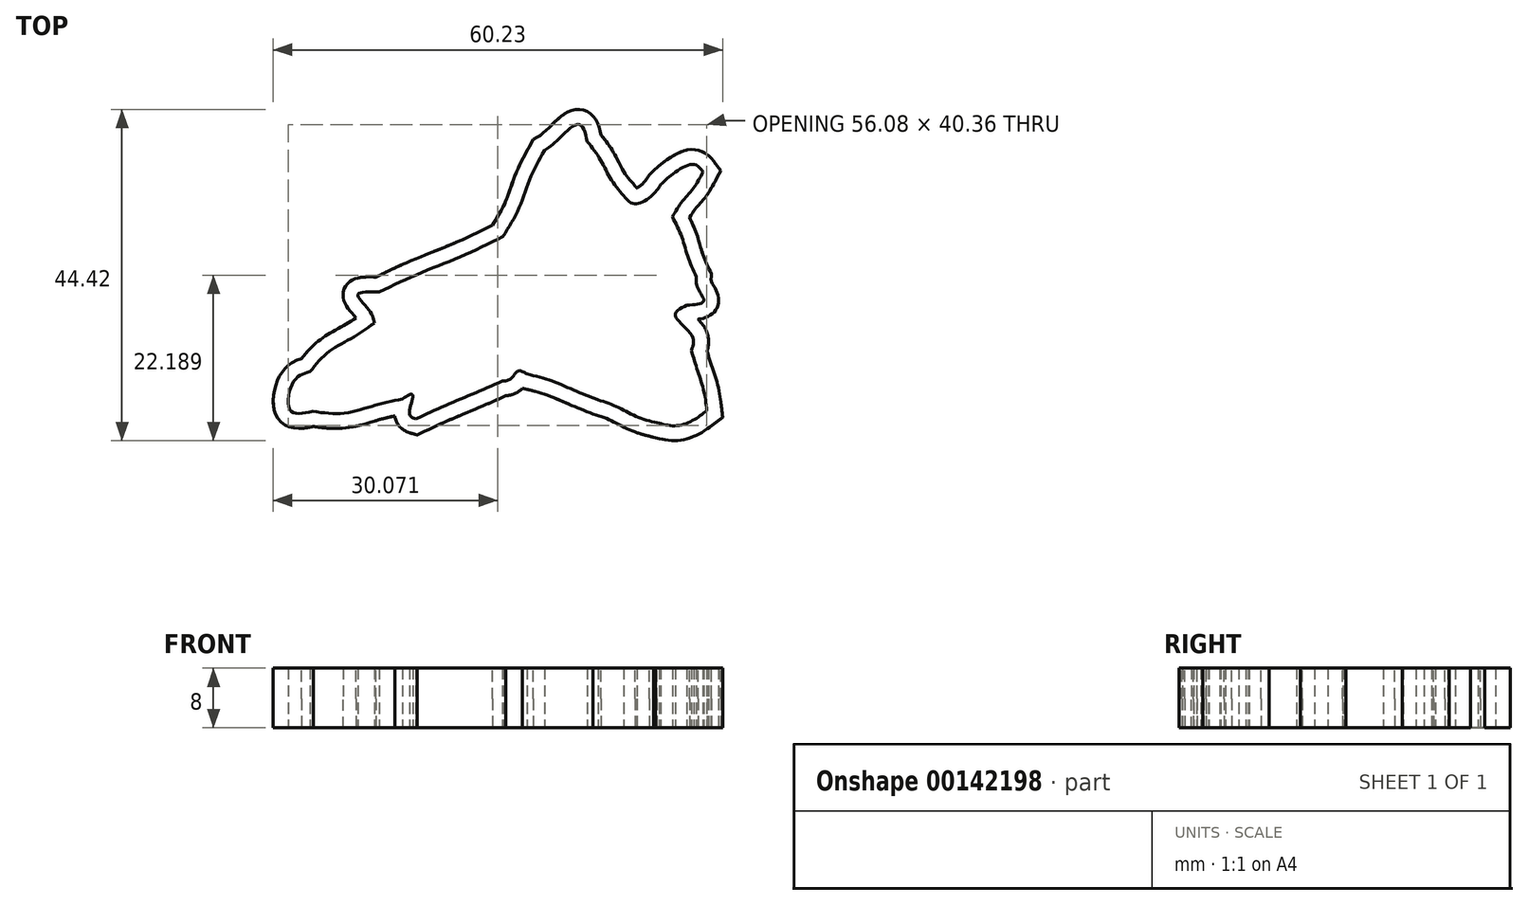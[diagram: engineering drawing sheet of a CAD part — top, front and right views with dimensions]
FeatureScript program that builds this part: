
annotation { "Feature Type Name" : "Feature", "Feature Type Description" : "" }
export const myFeature = defineFeature(function(context is Context, id is Id, definition is map)
    precondition{}
    {
        {
            var Q0;
            Q0=qCreatedBy(makeId("Top.planeOp"),FACE);
            var sketch = newSketch(context, id + "F0", { "sketchPlane" : qUnion([Q0])});
            skFitSpline(sketch, "E0", {"points": [v(207.98, -192.64) * mm, v(180.99, -184.62) * mm, v(155.3, -171.77) * mm, v(128.78, -161.9) * mm]});
            skFitSpline(sketch, "E1", {"points": [v(128.78, -161.9) * mm, v(97.41, -149.3) * mm, v(66.22, -136.29) * mm, v(33.65, -127.28) * mm]});
            skFitSpline(sketch, "E2", {"points": [v(33.65, -127.28) * mm, v(21.66, -123.25) * mm, v(11.66, -133.84) * mm, v(0.62, -136.7) * mm]});
            skFitSpline(sketch, "E3", {"points": [v(0.62, -136.7) * mm, v(-38.12, -153.64) * mm, v(-77.1, -170.06) * mm, v(-115.57, -187.57) * mm]});
            skFitSpline(sketch, "E4", {"points": [v(-115.57, -187.57) * mm, v(-123.77, -180.92) * mm, v(-119.85, -155.13) * mm, v(-133.48, -160.64) * mm]});
            skFitSpline(sketch, "E5", {"points": [v(-133.48, -160.64) * mm, v(-172.62, -170.05) * mm, v(-212.95, -179.94) * mm, v(-253.4, -177.34) * mm]});
            skFitSpline(sketch, "E6", {"points": [v(-253.4, -177.34) * mm, v(-283.5, -175.85) * mm, v(-278.66, -136.68) * mm, v(-257.19, -124.2) * mm]});
            skFitSpline(sketch, "E7", {"points": [v(-257.19, -124.2) * mm, v(-232.27, -97.76) * mm, v(-200.98, -79.07) * mm, v(-171.08, -59.07) * mm]});
            skFitSpline(sketch, "E8", {"points": [v(-171.08, -59.07) * mm, v(-177.57, -42.24) * mm, v(-192.94, -21.02) * mm, v(-164.68, -17.5) * mm]});
            skFitSpline(sketch, "E9", {"points": [v(-164.68, -17.5) * mm, v(-109.73, 8) * mm, v(-53.29, 30.82) * mm, v(1.22, 56.87) * mm]});
            skFitSpline(sketch, "E10", {"points": [v(1.22, 56.87) * mm, v(22.3, 94.12) * mm, v(37.5, 134.5) * mm, v(56.87, 172.55) * mm]});
            skFitSpline(sketch, "E11", {"points": [v(56.87, 172.55) * mm, v(71.2, 183.15) * mm, v(102.82, 207.47) * mm, v(114.38, 184.26) * mm]});
            skFitSpline(sketch, "E12", {"points": [v(114.38, 184.26) * mm, v(131.65, 160.66) * mm, v(145.7, 134.5) * mm, v(163.45, 111.5) * mm]});
            skFitSpline(sketch, "E13", {"points": [v(163.45, 111.5) * mm, v(178.1, 100.76) * mm, v(201, 112.12) * mm, v(212.98, 126.63) * mm]});
            skFitSpline(sketch, "E14", {"points": [v(212.98, 126.63) * mm, v(225.98, 138.5) * mm, v(255.9, 153.74) * mm, v(269.56, 143.47) * mm]});
            skFitSpline(sketch, "E15", {"points": [v(269.56, 143.47) * mm, v(257.2, 122.68) * mm, v(241.52, 103.8) * mm, v(228.38, 83.44) * mm]});
            skFitSpline(sketch, "E16", {"points": [v(228.38, 83.44) * mm, v(240.74, 57.28) * mm, v(249.34, 29.67) * mm, v(260.41, 3) * mm]});
            skFitSpline(sketch, "E17", {"points": [v(260.41, 3) * mm, v(262.58, -12.54) * mm, v(270.34, -29.44) * mm, v(247.92, -35.02) * mm]});
            skFitSpline(sketch, "E18", {"points": [v(247.92, -35.02) * mm, v(232.4, -48.68) * mm, v(254.9, -76.08) * mm, v(253.93, -95.71) * mm]});
            skFitSpline(sketch, "E19", {"points": [v(253.93, -95.71) * mm, v(261.93, -122.2) * mm, v(270.33, -149.05) * mm, v(274.63, -176.4) * mm]});
            skFitSpline(sketch, "E20", {"points": [v(274.63, -176.4) * mm, v(257.37, -188.55) * mm, v(233.43, -196.59) * mm, v(210.62, -193.22) * mm]});
            skLineSegment(sketch, "E21", {"start": v(210.62, -193.22) * mm, "end": v(207.98, -192.64) * mm});
            skLineSegment(sketch, "E22", {"start": v(207.98, -192.64) * mm, "end": v(207.98, -192.64) * mm});
            skLineSegment(sketch, "E23", {"start": v(207.98, -192.64) * mm, "end": v(210.62, -193.22) * mm});
            skSolve(sketch);
        }
        {
            var Q0;
            Q0 = qSketchRegion(id + "F0", true);
            extrude(context, id + "F1", {"entities" : qUnion([Q0]), "depth" : 38.9 * mm});
        }
        {
            var Q0;
            Q0=makeQuery(id+"F1.opExtrude","SWEPT_BODY",BODY,{"disambiguationData":[OSD([sQuery(id+"F0.wireOp",EDGE,"E0"),sQuery(id+"F0.wireOp",EDGE,"E1"),sQuery(id+"F0.wireOp",EDGE,"E2"),sQuery(id+"F0.wireOp",EDGE,"E3"),sQuery(id+"F0.wireOp",EDGE,"E4"),sQuery(id+"F0.wireOp",EDGE,"E5"),sQuery(id+"F0.wireOp",EDGE,"E6"),sQuery(id+"F0.wireOp",EDGE,"E7"),sQuery(id+"F0.wireOp",EDGE,"E8"),sQuery(id+"F0.wireOp",EDGE,"E9"),sQuery(id+"F0.wireOp",EDGE,"E10"),sQuery(id+"F0.wireOp",EDGE,"E11"),sQuery(id+"F0.wireOp",EDGE,"E12"),sQuery(id+"F0.wireOp",EDGE,"E13"),sQuery(id+"F0.wireOp",EDGE,"E14"),sQuery(id+"F0.wireOp",EDGE,"E15"),sQuery(id+"F0.wireOp",EDGE,"E16"),sQuery(id+"F0.wireOp",EDGE,"E17"),sQuery(id+"F0.wireOp",EDGE,"E18"),sQuery(id+"F0.wireOp",EDGE,"E19"),sQuery(id+"F0.wireOp",EDGE,"E20"),sQuery(id+"F0.wireOp",EDGE,"E23")])]});
            var Q1;
            Q1=qCreatedBy(makeId("Origin.pointOp"),VERTEX);
            transform(context, id + "F2", {"entities" : qUnion([Q0]), "transformType" : TransformType.SCALE_UNIFORMLY, "scale" : 0.1, "scalePoint" : qUnion([Q1]), "makeCopy" : false});
        }
        {
            var Q0;
            Q0=makeQuery(id+"F1.opExtrude","CAP_FACE",FACE,{"disambiguationData":[OSD([sQuery(id+"F0.wireOp",EDGE,"E0"),sQuery(id+"F0.wireOp",EDGE,"E1"),sQuery(id+"F0.wireOp",EDGE,"E2"),sQuery(id+"F0.wireOp",EDGE,"E3"),sQuery(id+"F0.wireOp",EDGE,"E4"),sQuery(id+"F0.wireOp",EDGE,"E5"),sQuery(id+"F0.wireOp",EDGE,"E6"),sQuery(id+"F0.wireOp",EDGE,"E7"),sQuery(id+"F0.wireOp",EDGE,"E8"),sQuery(id+"F0.wireOp",EDGE,"E9"),sQuery(id+"F0.wireOp",EDGE,"E10"),sQuery(id+"F0.wireOp",EDGE,"E11"),sQuery(id+"F0.wireOp",EDGE,"E12"),sQuery(id+"F0.wireOp",EDGE,"E13"),sQuery(id+"F0.wireOp",EDGE,"E14"),sQuery(id+"F0.wireOp",EDGE,"E15"),sQuery(id+"F0.wireOp",EDGE,"E16"),sQuery(id+"F0.wireOp",EDGE,"E17"),sQuery(id+"F0.wireOp",EDGE,"E18"),sQuery(id+"F0.wireOp",EDGE,"E19"),sQuery(id+"F0.wireOp",EDGE,"E20"),sQuery(id+"F0.wireOp",EDGE,"E23")])],"isStart":false});
            var Q1;
            Q1=makeQuery(id+"F1.opExtrude","CAP_FACE",FACE,{"disambiguationData":[OSD([sQuery(id+"F0.wireOp",EDGE,"E0"),sQuery(id+"F0.wireOp",EDGE,"E1"),sQuery(id+"F0.wireOp",EDGE,"E2"),sQuery(id+"F0.wireOp",EDGE,"E3"),sQuery(id+"F0.wireOp",EDGE,"E4"),sQuery(id+"F0.wireOp",EDGE,"E5"),sQuery(id+"F0.wireOp",EDGE,"E6"),sQuery(id+"F0.wireOp",EDGE,"E7"),sQuery(id+"F0.wireOp",EDGE,"E8"),sQuery(id+"F0.wireOp",EDGE,"E9"),sQuery(id+"F0.wireOp",EDGE,"E10"),sQuery(id+"F0.wireOp",EDGE,"E11"),sQuery(id+"F0.wireOp",EDGE,"E12"),sQuery(id+"F0.wireOp",EDGE,"E13"),sQuery(id+"F0.wireOp",EDGE,"E14"),sQuery(id+"F0.wireOp",EDGE,"E15"),sQuery(id+"F0.wireOp",EDGE,"E16"),sQuery(id+"F0.wireOp",EDGE,"E17"),sQuery(id+"F0.wireOp",EDGE,"E18"),sQuery(id+"F0.wireOp",EDGE,"E19"),sQuery(id+"F0.wireOp",EDGE,"E20"),sQuery(id+"F0.wireOp",EDGE,"E23")])],"isStart":true});
            shell(context, id + "F3", {"entities" : qUnion([Q0, Q1]), "thickness" : 2 * mm, "oppositeDirection" : true});
        }
        {
            var Q0;
            Q0=qCreatedBy(makeId("Top.planeOp"),FACE);
            cPlane(context, id + "F4", {"entities" : qUnion([Q0]), "cplaneType" : CPlaneType.OFFSET, "offset" : 8 * mm, "width" : 150 * mm, "height" : 150 * mm});
        }
        {
            var Q0;
            Q0=makeQuery(id+"F1.opExtrude","CAP_FACE",FACE,{"disambiguationData":[OSD([sQuery(id+"F0.wireOp",EDGE,"E0"),sQuery(id+"F0.wireOp",EDGE,"E1"),sQuery(id+"F0.wireOp",EDGE,"E2"),sQuery(id+"F0.wireOp",EDGE,"E3"),sQuery(id+"F0.wireOp",EDGE,"E4"),sQuery(id+"F0.wireOp",EDGE,"E5"),sQuery(id+"F0.wireOp",EDGE,"E6"),sQuery(id+"F0.wireOp",EDGE,"E7"),sQuery(id+"F0.wireOp",EDGE,"E8"),sQuery(id+"F0.wireOp",EDGE,"E9"),sQuery(id+"F0.wireOp",EDGE,"E10"),sQuery(id+"F0.wireOp",EDGE,"E11"),sQuery(id+"F0.wireOp",EDGE,"E12"),sQuery(id+"F0.wireOp",EDGE,"E13"),sQuery(id+"F0.wireOp",EDGE,"E14"),sQuery(id+"F0.wireOp",EDGE,"E15"),sQuery(id+"F0.wireOp",EDGE,"E16"),sQuery(id+"F0.wireOp",EDGE,"E17"),sQuery(id+"F0.wireOp",EDGE,"E18"),sQuery(id+"F0.wireOp",EDGE,"E19"),sQuery(id+"F0.wireOp",EDGE,"E20"),sQuery(id+"F0.wireOp",EDGE,"E23")])],"isStart":false});
            var Q1;
            Q1=qCreatedBy(id+"F4.planeOp",FACE);
            extrude(context, id + "F5", {"entities" : qUnion([Q0]), "operationType" : NewBodyOperationType.ADD, "endBound" : BoundingType.UP_TO_SURFACE, "endBoundEntityFace" : qUnion([Q1]), "depth" : 2.68 * mm});
        }
    });
